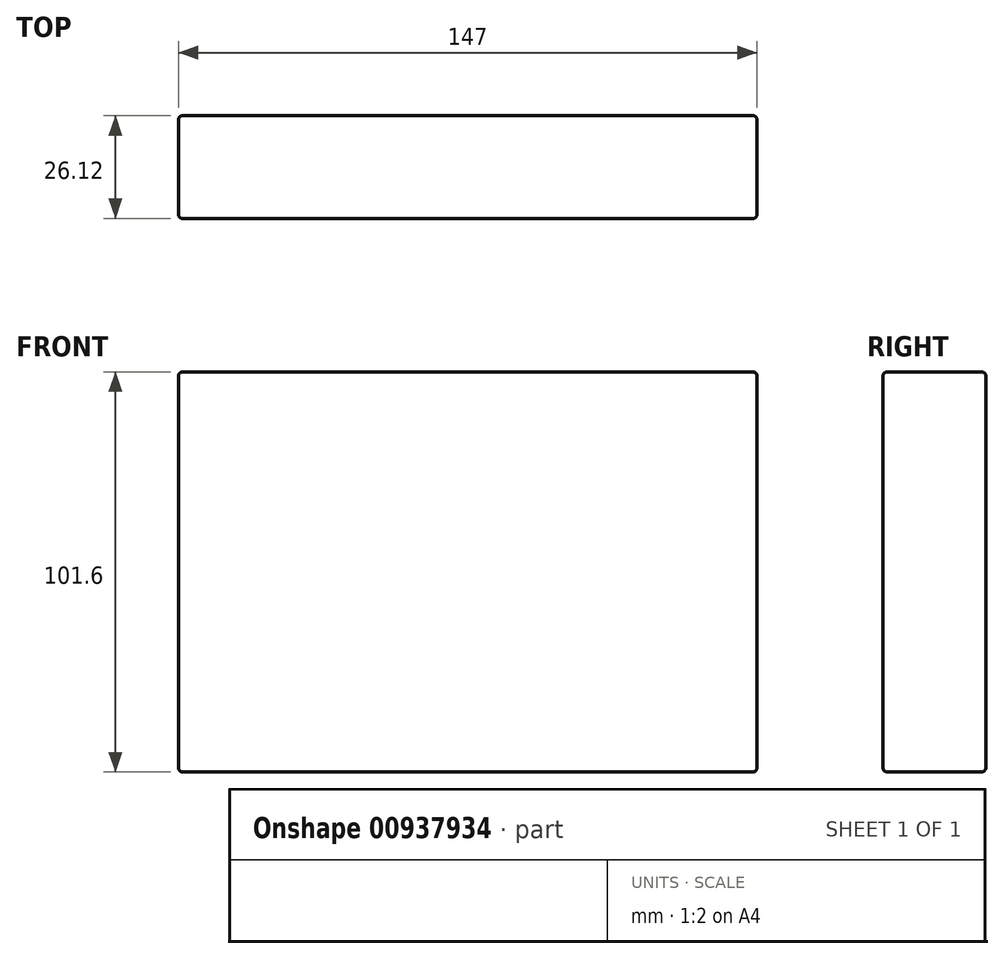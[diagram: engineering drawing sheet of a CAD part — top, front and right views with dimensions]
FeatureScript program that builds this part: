
annotation { "Feature Type Name" : "Feature", "Feature Type Description" : "" }
export const myFeature = defineFeature(function(context is Context, id is Id, definition is map)
    precondition{}
    {
        {
            var Q0;
            Q0=qCreatedBy(makeId("Top.planeOp"),FACE);
            var sketch = newSketch(context, id + "F0", { "sketchPlane" : qUnion([Q0])});
            skLineSegment(sketch, "E0.bottom", {"start": v(73.5, -13.05) * mm, "end": v(-73.5, -13.06) * mm});
            skLineSegment(sketch, "E0.top", {"start": v(73.5, 13.06) * mm, "end": v(-73.5, 13.05) * mm});
            skLineSegment(sketch, "E0.left", {"start": v(73.5, -13.05) * mm, "end": v(73.5, 13.06) * mm});
            skLineSegment(sketch, "E0.right", {"start": v(-73.5, -13.06) * mm, "end": v(-73.5, 13.05) * mm});
            skPoint(sketch, "E0.middle", {"position": v(0, 0) * mm});
            skSolve(sketch);
        }
        {
            var Q0;
            Q0=makeQuery(id+"F0.imprint","IMPRINT",FACE,{"disambiguationData":[TD([[makeQuery(id+"F0.imprint","IMPRINT",EDGE,{"derivedFrom":sQuery(id+"F0.wireOp",EDGE,"E0.bottom")}),-1.0]])]});
            extrude(context, id + "F1", {"entities" : qUnion([Q0]), "endBound" : BoundingType.SYMMETRIC, "depth" : 101.6 * mm, "offsetDistance" : 25 * mm});
        }
        {
            var Q0;
            Q0=makeQuery(id+"F1.opExtrude","CAP_FACE",FACE,{"disambiguationData":[OSD([sQuery(id+"F0.wireOp",EDGE,"E0.bottom"),sQuery(id+"F0.wireOp",EDGE,"E0.top"),sQuery(id+"F0.wireOp",EDGE,"E0.left"),sQuery(id+"F0.wireOp",EDGE,"E0.right")])],"isStart":false});
            var Q1;
            Q1=makeQuery(id+"F1.opExtrude","SWEPT_FACE",FACE,{"disambiguationData":[OSD([sQuery(id+"F0.wireOp",EDGE,"E0.left")])]});
            var Q2;
            Q2=makeQuery(id+"F1.opExtrude","SWEPT_FACE",FACE,{"disambiguationData":[OSD([sQuery(id+"F0.wireOp",EDGE,"E0.bottom")])]});
            var Q3;
            Q3=makeQuery(id+"F1.opExtrude","CAP_FACE",FACE,{"disambiguationData":[OSD([sQuery(id+"F0.wireOp",EDGE,"E0.bottom"),sQuery(id+"F0.wireOp",EDGE,"E0.top"),sQuery(id+"F0.wireOp",EDGE,"E0.left"),sQuery(id+"F0.wireOp",EDGE,"E0.right")])],"isStart":true});
            var Q4;
            Q4=makeQuery(id+"F1.opExtrude","SWEPT_FACE",FACE,{"disambiguationData":[OSD([sQuery(id+"F0.wireOp",EDGE,"E0.top")])]});
            var Q5;
            Q5=makeQuery(id+"F1.opExtrude","SWEPT_FACE",FACE,{"disambiguationData":[OSD([sQuery(id+"F0.wireOp",EDGE,"E0.right")])]});
            fillet(context, id + "F2", {"entities" : qUnion([Q0, Q1, Q2, Q3, Q4, Q5]), "radius" : 1 * mm, "tangentPropagation" : true, "allowEdgeOverflow" : false});
        }
    });
